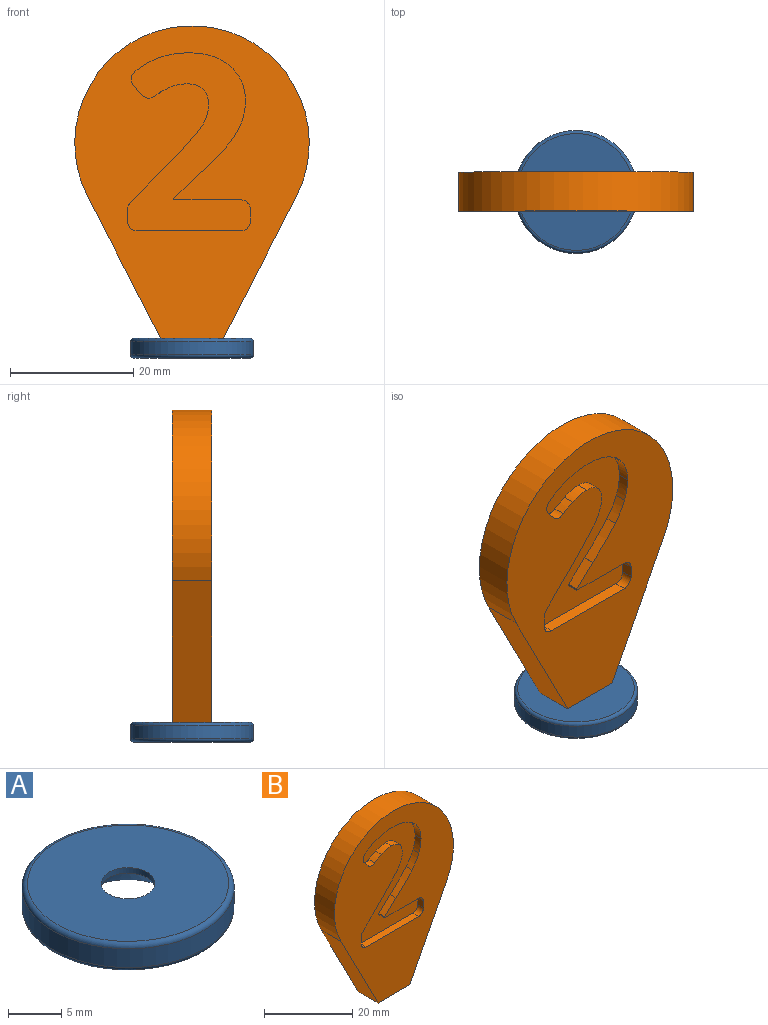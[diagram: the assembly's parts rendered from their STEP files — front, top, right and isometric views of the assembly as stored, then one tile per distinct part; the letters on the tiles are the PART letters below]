
ASSEMBLY  parts=2 mates=1
PART A: 7 faces, bbox 21.6x21.6x3.2 mm
  f0: cylinder r=2.54mm len=5.08mm, axis (0,0,-1), area 10.1mm2, adj f2,f4
  f1: cylinder r=9.99mm len=19.99mm, axis (0,0,-1), area 135.6mm2, adj f5,f6
  f2: plane 18.97x18.97mm, normal (0,0,1), area 262.5mm2, adj f0,f6
  f3: plane 18.97x18.97mm, normal (0,0,-1), area 201.7mm2, adj f4,f5
  f4: cone r=5.08mm half-angle=45deg, axis (0,0,-1), area 86mm2, adj f0,f3
  f5: torus R=9.49mm, axis (0,0,1), area 49.2mm2, adj f1,f3
  f6: torus R=9.49mm, axis (0,0,1), area 49.2mm2, adj f1,f2
PART B: 70 faces, bbox 38.1x6.4x50.8 mm
  f0: plane 1.91x1.9mm, normal (-1,0,0), area 3.6mm2, adj f30,f31,f61,f68
  f1: plane 16.78x1.91mm, normal (0,0,1), area 32mm2, adj f24,f31,f61,f68
  f2: plane 1.96x1.91mm, normal (1,0,0), area 3.7mm2, adj f24,f25,f61,f68
  f3: plane 6.78x6.71mm, normal (0.71,0,-0.7), area 18.2mm2, adj f19,f25,f61,f68
  f4: extruded ~2.33x1.91mm, area 5.2mm2, adj f5,f19,f61,f68
  f5: extruded ~2.22x1.91mm, area 4.3mm2, adj f4,f6,f61,f68
  f6: extruded ~2.56x1.91mm, area 5.4mm2, adj f5,f7,f61,f68
  f7: extruded ~2.53x1.91mm, area 5.2mm2, adj f6,f8,f61,f68
  f8: extruded ~3.22x1.91mm, area 6.4mm2, adj f7,f20,f61,f68
  f9: plane 1.91x1.49mm, normal (0.76,0,0.65), area 3.7mm2, adj f26,f27,f61,f68
  f10: extruded ~3.03x1.91mm, area 6.2mm2, adj f11,f21,f61,f68
  f11: extruded ~3.67x1.91mm, area 7mm2, adj f10,f12,f61,f68
  f12: extruded ~4.72x1.91mm, area 9.3mm2, adj f11,f13,f61,f68
  f13: extruded ~3.18x2.73mm, area 8.1mm2, adj f12,f14,f61,f68
  f14: extruded ~4.02x1.91mm, area 8.1mm2, adj f13,f15,f61,f68
  f15: extruded ~3.7x1.91mm, area 7.2mm2, adj f14,f16,f61,f68
  f16: extruded ~3.54x2.15mm, area 7.9mm2, adj f15,f22,f61,f68
  f17: plane 3.67x3.45mm, normal (-0.69,0,0.73), area 9.6mm2, adj f23,f28,f61,f68
  f18: plane 10.85x1.91mm, normal (0,0,-1), area 20.7mm2, adj f23,f30,f61,f68
  f19: extruded ~4.52x4.16mm, area 11.7mm2, adj f3,f4,f61,f68
  f20: extruded ~2.1x1.91mm, area 4.7mm2, adj f8,f26,f61,f68
  f21: extruded ~2.22x1.91mm, area 5.1mm2, adj f10,f27,f61,f68
  f22: extruded ~5.17x5.12mm, area 13.9mm2, adj f16,f28,f61,f68
  f23: plane 1.91x0.27mm, normal (-1,0,0), area 0.5mm2, adj f17,f18,f61,f68
  f24: cylinder r=1.59mm len=1.91mm, axis (0,-1,0), area 4.8mm2, adj f1,f2,f61,f68
  f25: cylinder r=1.59mm len=1.91mm, axis (0,-1,0), area 2.4mm2, adj f2,f3,f61,f68
  f26: cylinder r=1.59mm len=2.14mm, axis (0,1,0), area 4.5mm2, adj f9,f20,f61,f68
  f27: cylinder r=1.59mm len=2.28mm, axis (0,1,0), area 4.9mm2, adj f9,f21,f61,f68
  f28: cylinder r=1.59mm len=1.91mm, axis (0,1,0), area 0mm2, adj f17,f22,f61,f68
  f29: cylinder r=1.59mm len=1.91mm, axis (0,1,0), area 0mm2, adj f55,f56,f60,f69
  f30: cylinder r=1.59mm len=1.91mm, axis (0,-1,0), area 4.8mm2, adj f0,f18,f61,f68
  f31: cylinder r=1.59mm len=1.91mm, axis (0,-1,0), area 4.8mm2, adj f0,f1,f61,f68
  f32: cylinder r=19.05mm len=38.1mm, axis (0,1,0), area 495.1mm2, adj f33,f59,f60,f61
  f33: plane 23.03x11.86mm, normal (-0.89,0,-0.46), area 164.5mm2, adj f32,f34,f60,f61
  f34: plane 10.16x6.35mm, normal (0,0,-1), area 64.5mm2, adj f33,f59,f60,f61
  f35: plane 1.91x1.9mm, normal (-1,0,0), area 3.6mm2, adj f60,f66,f67,f69
  f36: plane 16.78x1.91mm, normal (0,0,1), area 32mm2, adj f60,f62,f67,f69
  f37: plane 1.96x1.91mm, normal (1,0,0), area 3.7mm2, adj f60,f62,f63,f69
  f38: plane 6.78x6.71mm, normal (0.71,0,-0.7), area 18.2mm2, adj f39,f60,f63,f69
  f39: extruded ~4.52x4.16mm, area 11.7mm2, adj f38,f40,f60,f69
  f40: extruded ~2.33x1.91mm, area 5.2mm2, adj f39,f41,f60,f69
  f41: extruded ~2.22x1.91mm, area 4.3mm2, adj f40,f42,f60,f69
  f42: extruded ~2.56x1.91mm, area 5.4mm2, adj f41,f43,f60,f69
  f43: extruded ~2.53x1.91mm, area 5.2mm2, adj f42,f44,f60,f69
  f44: extruded ~3.22x1.91mm, area 6.4mm2, adj f43,f45,f60,f69
  f45: extruded ~2.1x1.91mm, area 4.7mm2, adj f44,f60,f64,f69
  f46: plane 1.91x1.49mm, normal (0.76,0,0.65), area 3.7mm2, adj f60,f64,f65,f69
  f47: extruded ~2.22x1.91mm, area 5.1mm2, adj f48,f60,f65,f69
  f48: extruded ~3.03x1.91mm, area 6.2mm2, adj f47,f49,f60,f69
  f49: extruded ~3.67x1.91mm, area 7mm2, adj f48,f50,f60,f69
  f50: extruded ~4.72x1.91mm, area 9.3mm2, adj f49,f51,f60,f69
  f51: extruded ~3.18x2.73mm, area 8.1mm2, adj f50,f52,f60,f69
  f52: extruded ~4.02x1.91mm, area 8.1mm2, adj f51,f53,f60,f69
  f53: extruded ~3.7x1.91mm, area 7.2mm2, adj f52,f54,f60,f69
  f54: extruded ~3.54x2.15mm, area 7.9mm2, adj f53,f55,f60,f69
  f55: extruded ~5.17x5.12mm, area 13.9mm2, adj f29,f54,f60,f69
  f56: plane 3.67x3.45mm, normal (-0.69,0,0.73), area 9.6mm2, adj f29,f57,f60,f69
  f57: plane 1.91x0.27mm, normal (-1,0,0), area 0.5mm2, adj f56,f58,f60,f69
  f58: plane 10.85x1.91mm, normal (0,0,-1), area 20.7mm2, adj f57,f60,f66,f69
  f59: plane 23.03x11.86mm, normal (0.89,0,-0.46), area 164.5mm2, adj f32,f34,f60,f61
  f60: plane 50.8x38.1mm, normal (0,-1,0), area 1096.6mm2, adj f29,f32,f33,f34,f35,f36,f37,f38
  f61: plane 50.8x38.1mm, normal (0,1,0), area 1096.6mm2, adj f0,f1,f2,f3,f4,f5,f6,f7
  f62: cylinder r=1.59mm len=1.91mm, axis (0,-1,0), area 4.8mm2, adj f36,f37,f60,f69
  f63: cylinder r=1.59mm len=1.91mm, axis (0,-1,0), area 2.4mm2, adj f37,f38,f60,f69
  f64: cylinder r=1.59mm len=2.14mm, axis (0,1,0), area 4.5mm2, adj f45,f46,f60,f69
  f65: cylinder r=1.59mm len=2.28mm, axis (0,1,0), area 4.9mm2, adj f46,f47,f60,f69
  f66: cylinder r=1.59mm len=1.91mm, axis (0,-1,0), area 4.8mm2, adj f35,f58,f60,f69
  f67: cylinder r=1.59mm len=1.91mm, axis (0,-1,0), area 4.8mm2, adj f35,f36,f60,f69
  f68: plane 28.95x19.95mm, normal (0,1,0), area 300.7mm2, adj f0,f1,f2,f3,f4,f5,f6,f7
  f69: plane 28.95x19.95mm, normal (0,-1,0), area 300.7mm2, adj f29,f35,f36,f37,f38,f39,f40,f41
PLACE A t=(0.04,-0.1,-1.77)mm
PLACE B t=(0.04,-0.1,1.41)mm
MATE revolute B.f34 <-> A.f0  axis (0,0,-1) through (0.04,-0.1,1.41)mm
